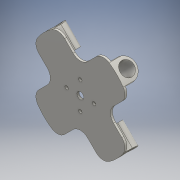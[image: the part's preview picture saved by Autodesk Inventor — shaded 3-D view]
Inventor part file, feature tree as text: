
AUTODESK INVENTOR PART (.ipt)
format: ipt  version: 2016 (Build 200138000, 138)  size: 246,784 bytes
history: native  units: mm
features: extrude x5, sketch x5, fillet x3, pattern_circular x1
ambient origin geometry x8: Origin, YZ Plane, XZ Plane, XY Plane, X Axis, Y Axis, Z Axis, Center Point
bodies: Body1 (feature_tree)
feature tree (14):
  extrude  "Extrusion2"  Depth=10.0mm
  extrude  "Extrusion3"  TaperAngle=45.0deg  [1 undecoded]
  fillet  "Fillet1"  Radius=25.0mm
  extrude  "Extrusion4"  Depth=15.0mm
  pattern_circular  "Circular Pattern1"  Count=4 Angle=360.0deg
  extrude  "Extrusion5"  Depth=15.0mm
  extrude  "Extrusion6"  Depth=15.0mm
  fillet  "Fillet2"  Radius=20.0mm
  fillet  "Fillet3"  Radius=5.0mm
  sketch  "Sketch1"  dims[d0=150.0mm d3=10.0mm]
  sketch  "Sketch3"  dims[d4=3.0mm d5=0.0mm d12=45.0deg d13=25.0mm d14=0.0mm]
  sketch  "Sketch5"  dims[d15=15.0mm d16=20.0mm]
  sketch  "Sketch6"  dims[d17=25.0mm d18=0.0mm d19=40.0mm d20=360.0deg]
  sketch  "Sketch7"  dims[d22=30.0mm d23=15.0mm d24=15.0mm d25=20.0mm d26=5.0mm d27=40.0mm d29=360.0deg d31=25.0mm d32=0.0mm d33=45.0deg d34=45.0deg d35=40.0mm d37=360.0deg d39=25.0mm d40=0.0mm d41=15.0mm d42=15.0mm]
note: 1 required parameter value undecoded (feature->parameter linkage not recoverable at this tier; creation-order binding heuristic only, values carry confidence <= 0.55)
